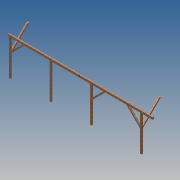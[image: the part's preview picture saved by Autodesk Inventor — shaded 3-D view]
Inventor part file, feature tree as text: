
AUTODESK INVENTOR PART (.ipt)
format: ipt  version: 2013 (Build 170138000, 138)  size: 199,168 bytes
history: native  units: in
note: dims shown in document units (in); Inventor stores cm internally (conversion verified against a paired STEP export)
features: extrude x6, sketch x6
ambient origin geometry x8: Origin, YZ Plane, XZ Plane, XY Plane, X Axis, Y Axis, Z Axis, Center Point
bodies: Solid1 (feature_tree)
feature tree (12):
  extrude  "Extrusion1"  Depth=90.5in
  extrude  "Extrusion4"  Depth=369.0in
  extrude  "Extrusion5"  Depth=3.5in
  extrude  "Extrusion7"  Depth=3.5in
  extrude  "Extrusion8"  Depth=3.5in
  extrude  "Extrusion9"  Depth=30.0in
  sketch  "Sketch1"  dims[d0=3.5in d1=90.5in]
  sketch  "Sketch4"  dims[d2=30.0in d3=369.0in]
  sketch  "Sketch5"  dims[d4=5.5in d5=3.5in]
  sketch  "Sketch7"  dims[d6=127.25in d7=3.5in]
  sketch  "Sketch8"  dims[d8=103.0in d9=3.5in]
  sketch  "Sketch9"  dims[d10=103.25in d12=30.0in d15=3.5in d16=0.0in d23=135.0deg d24=30.0in d25=3.5in d27=3.5in d28=0.0in d29=1.0in d31=1.0in d32=0.0in d42=3.5in d43=0.0in d48=3.5in d49=0.0in d50=187.25in d51=0.5in d52=0.0in d53=0.9689in d54=6.0936in d55=6.094in d56=0.9689in]
